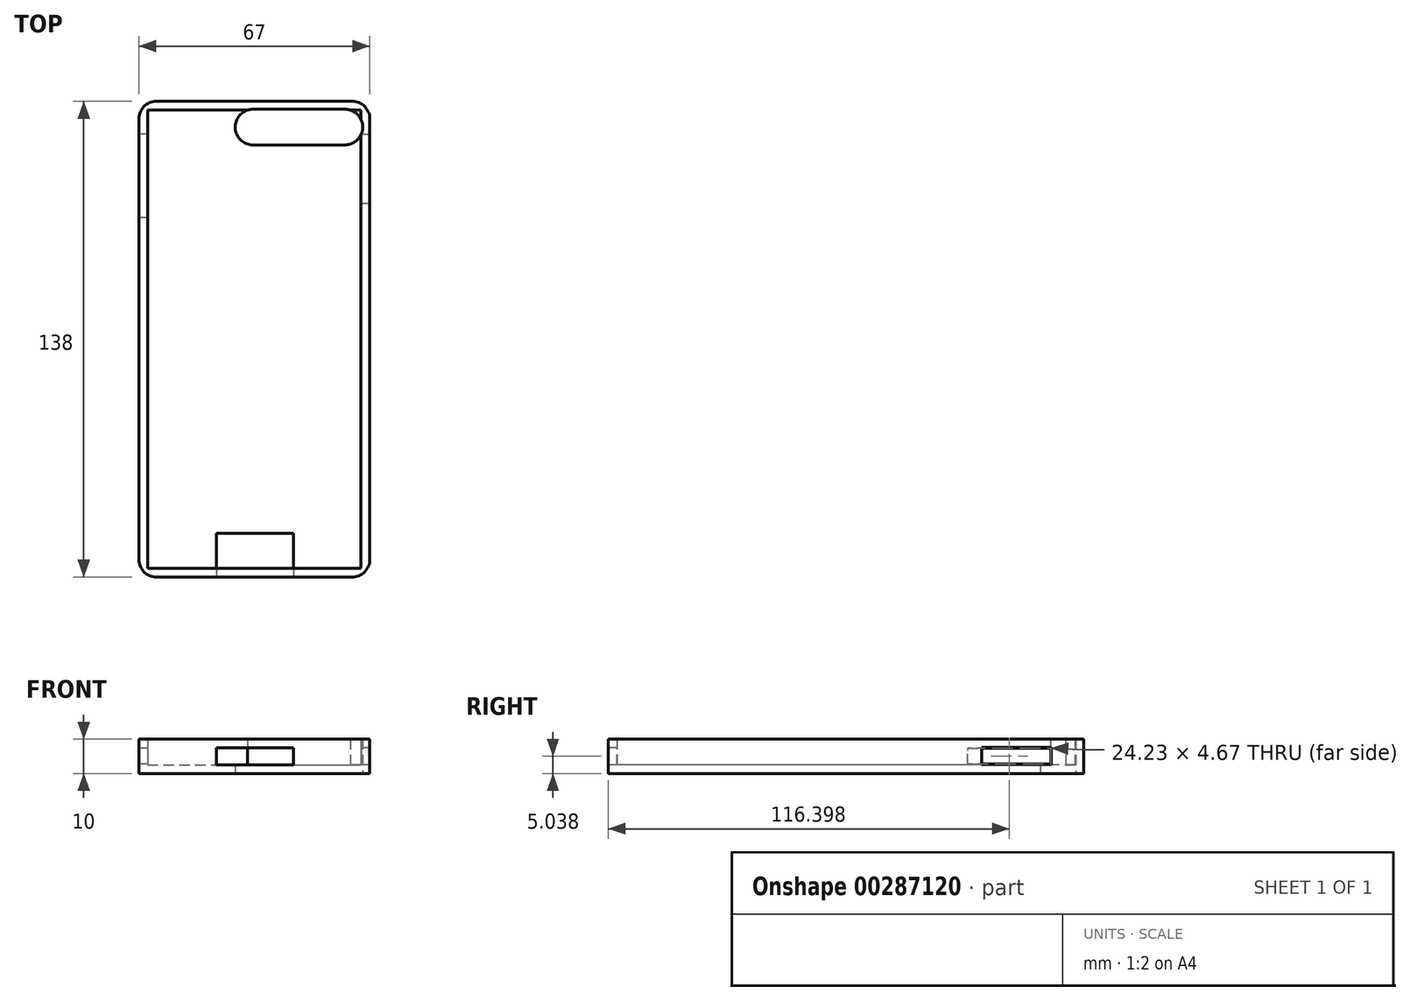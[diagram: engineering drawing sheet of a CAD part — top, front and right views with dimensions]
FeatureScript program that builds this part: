
annotation { "Feature Type Name" : "Feature", "Feature Type Description" : "" }
export const myFeature = defineFeature(function(context is Context, id is Id, definition is map)
    precondition{}
    {
        {
            var Q0;
            Q0=qCreatedBy(makeId("Top.planeOp"),FACE);
            var sketch = newSketch(context, id + "F0", { "sketchPlane" : qUnion([Q0])});
            skLineSegment(sketch, "E0.bottom", {"start": v(-44.89, 63.82) * mm, "end": v(22.11, 63.82) * mm});
            skLineSegment(sketch, "E0.top", {"start": v(-44.89, -74.18) * mm, "end": v(22.11, -74.18) * mm});
            skLineSegment(sketch, "E0.left", {"start": v(-44.89, 63.82) * mm, "end": v(-44.89, -74.18) * mm});
            skLineSegment(sketch, "E0.right", {"start": v(22.11, 63.82) * mm, "end": v(22.11, -74.18) * mm});
            skSolve(sketch);
        }
        {
            var Q0;
            Q0=makeQuery(id+"F0.imprint","IMPRINT",FACE,{"disambiguationData":[TD([[makeQuery(id+"F0.imprint","IMPRINT",EDGE,{"derivedFrom":sQuery(id+"F0.wireOp",EDGE,"E0.bottom")}),-1.0]])]});
            extrude(context, id + "F1", {"entities" : qUnion([Q0]), "depth" : 10 * mm});
        }
        {
            var Q0;
            Q0=makeQuery(id+"F1.opExtrude","CAP_FACE",FACE,{"disambiguationData":[OSD([sQuery(id+"F0.wireOp",EDGE,"E0.bottom"),sQuery(id+"F0.wireOp",EDGE,"E0.top"),sQuery(id+"F0.wireOp",EDGE,"E0.left"),sQuery(id+"F0.wireOp",EDGE,"E0.right")])],"isStart":false});
            shell(context, id + "F2", {"entities" : qUnion([Q0]), "thickness" : 2.54 * mm});
        }
        {
            var Q0;
            Q0=makeQuery(id+"F1.opExtrude","SWEPT_EDGE",EDGE,{"disambiguationData":[OSD([sQuery(id+"F0.wireOp",EDGE,"E0.bottom"),sQuery(id+"F0.wireOp",EDGE,"E0.left")])]});
            fillet(context, id + "F3", {"entities" : qUnion([Q0]), "radius" : 5.08 * mm, "tangentPropagation" : true, "allowEdgeOverflow" : false});
        }
        {
            var Q0;
            Q0=makeQuery(id+"F1.opExtrude","SWEPT_EDGE",EDGE,{"disambiguationData":[OSD([sQuery(id+"F0.wireOp",EDGE,"E0.bottom"),sQuery(id+"F0.wireOp",EDGE,"E0.right")])]});
            fillet(context, id + "F4", {"entities" : qUnion([Q0]), "radius" : 5.08 * mm, "tangentPropagation" : true, "allowEdgeOverflow" : false});
        }
        {
            var Q0;
            Q0=makeQuery(id+"F1.opExtrude","SWEPT_EDGE",EDGE,{"disambiguationData":[OSD([sQuery(id+"F0.wireOp",EDGE,"E0.top"),sQuery(id+"F0.wireOp",EDGE,"E0.right")])]});
            fillet(context, id + "F5", {"entities" : qUnion([Q0]), "radius" : 5.08 * mm, "tangentPropagation" : true, "allowEdgeOverflow" : false});
        }
        {
            var Q0;
            Q0=makeQuery(id+"F1.opExtrude","SWEPT_EDGE",EDGE,{"disambiguationData":[OSD([sQuery(id+"F0.wireOp",EDGE,"E0.top"),sQuery(id+"F0.wireOp",EDGE,"E0.left")])]});
            fillet(context, id + "F6", {"entities" : qUnion([Q0]), "radius" : 5.08 * mm, "tangentPropagation" : true, "allowEdgeOverflow" : false});
        }
        {
            var Q0;
            Q0=makeQuery(id+"F1.opExtrude","CAP_FACE",FACE,{"disambiguationData":[OSD([sQuery(id+"F0.wireOp",EDGE,"E0.bottom"),sQuery(id+"F0.wireOp",EDGE,"E0.top"),sQuery(id+"F0.wireOp",EDGE,"E0.left"),sQuery(id+"F0.wireOp",EDGE,"E0.right")])],"isStart":true});
            var sketch = newSketch(context, id + "F7", { "sketchPlane" : qUnion([Q0])});
            skLineSegment(sketch, "E1.bottom", {"start": v(14.88, -61.52) * mm, "end": v(-11.74, -61.52) * mm});
            skLineSegment(sketch, "E1.top", {"start": v(14.88, -51.16) * mm, "end": v(-11.74, -51.16) * mm});
            skLineSegment(sketch, "E1.left", {"start": v(14.88, -61.52) * mm, "end": v(14.88, -51.16) * mm});
            skLineSegment(sketch, "E1.right", {"start": v(-11.74, -61.52) * mm, "end": v(-11.74, -51.16) * mm});
            skArc(sketch, "E2", {"start": v(14.88, -61.52) * mm, "mid": v(20.06, -56.34) * mm, "end": v(14.88, -51.16) * mm});
            skArc(sketch, "E3", {"start": v(-11.74, -51.16) * mm, "mid": v(-16.92, -56.34) * mm, "end": v(-11.74, -61.52) * mm});
            skSolve(sketch);
        }
        {
            var Q0;
            Q0=makeQuery(id+"F7.imprint","IMPRINT",FACE,{"disambiguationData":[TD([[makeQuery(id+"F7.imprint","IMPRINT",EDGE,{"derivedFrom":sQuery(id+"F7.wireOp",EDGE,"E1.bottom")}),-1.0]])]});
            var Q1;
            Q1=makeQuery(id+"F7.imprint","IMPRINT",FACE,{"disambiguationData":[TD([[makeQuery(id+"F7.imprint","IMPRINT",EDGE,{"derivedFrom":sQuery(id+"F7.wireOp",EDGE,"E1.left")}),-1.0]])]});
            var Q2;
            Q2=makeQuery(id+"F7.imprint","IMPRINT",FACE,{"disambiguationData":[TD([[makeQuery(id+"F7.imprint","IMPRINT",EDGE,{"derivedFrom":sQuery(id+"F7.wireOp",EDGE,"E1.right")}),1.0]])]});
            extrude(context, id + "F8", {"entities" : qUnion([Q0, Q1, Q2]), "operationType" : NewBodyOperationType.REMOVE, "oppositeDirection" : true, "depth" : 25.4 * mm});
        }
        {
            var Q0;
            Q0=makeQuery(id+"F1.opExtrude","SWEPT_FACE",FACE,{"disambiguationData":[OSD([sQuery(id+"F0.wireOp",EDGE,"E0.top")])]});
            var sketch = newSketch(context, id + "F9", { "sketchPlane" : qUnion([Q0])});
            skLineSegment(sketch, "E4.bottom", {"start": v(-22.44, 7.43) * mm, "end": v(0, 7.43) * mm});
            skLineSegment(sketch, "E4.top", {"start": v(-22.44, 2.48) * mm, "end": v(0, 2.48) * mm});
            skLineSegment(sketch, "E4.left", {"start": v(-22.44, 7.43) * mm, "end": v(-22.44, 2.48) * mm});
            skLineSegment(sketch, "E4.right", {"start": v(0, 7.43) * mm, "end": v(0, 2.48) * mm});
            skSolve(sketch);
        }
        {
            var Q0;
            Q0=makeQuery(id+"F9.imprint","IMPRINT",FACE,{"disambiguationData":[TD([[makeQuery(id+"F9.imprint","IMPRINT",EDGE,{"derivedFrom":sQuery(id+"F9.wireOp",EDGE,"E4.bottom")}),-1.0]])]});
            extrude(context, id + "F10", {"entities" : qUnion([Q0]), "operationType" : NewBodyOperationType.REMOVE, "endBound" : BoundingType.SYMMETRIC, "oppositeDirection" : true, "depth" : 25.4 * mm});
        }
        {
            var Q0;
            Q0=makeQuery(id+"F1.opExtrude","SWEPT_FACE",FACE,{"disambiguationData":[OSD([sQuery(id+"F0.wireOp",EDGE,"E0.left")])]});
            var sketch = newSketch(context, id + "F11", { "sketchPlane" : qUnion([Q0])});
            skLineSegment(sketch, "E5.bottom", {"start": v(-54.33, 2.7) * mm, "end": v(-30.1, 2.7) * mm});
            skLineSegment(sketch, "E5.top", {"start": v(-54.33, 7.37) * mm, "end": v(-30.1, 7.37) * mm});
            skLineSegment(sketch, "E5.left", {"start": v(-54.33, 2.7) * mm, "end": v(-54.33, 7.37) * mm});
            skLineSegment(sketch, "E5.right", {"start": v(-30.1, 2.7) * mm, "end": v(-30.1, 7.37) * mm});
            skSolve(sketch);
        }
        {
            var Q0;
            Q0=makeQuery(id+"F11.imprint","IMPRINT",FACE,{"disambiguationData":[TD([[makeQuery(id+"F11.imprint","IMPRINT",EDGE,{"derivedFrom":sQuery(id+"F11.wireOp",EDGE,"E5.bottom")}),1.0]])]});
            extrude(context, id + "F12", {"entities" : qUnion([Q0]), "operationType" : NewBodyOperationType.REMOVE, "oppositeDirection" : true, "depth" : 25.4 * mm});
        }
        {
            var Q0;
            Q0=makeQuery(id+"F1.opExtrude","SWEPT_FACE",FACE,{"disambiguationData":[OSD([sQuery(id+"F0.wireOp",EDGE,"E0.right")])]});
            var sketch = newSketch(context, id + "F13", { "sketchPlane" : qUnion([Q0])});
            skLineSegment(sketch, "E6.bottom", {"start": v(54.36, 7.58) * mm, "end": v(34.25, 7.58) * mm});
            skLineSegment(sketch, "E6.top", {"start": v(54.36, 2.62) * mm, "end": v(34.25, 2.62) * mm});
            skLineSegment(sketch, "E6.left", {"start": v(54.36, 7.58) * mm, "end": v(54.36, 2.62) * mm});
            skLineSegment(sketch, "E6.right", {"start": v(34.25, 7.58) * mm, "end": v(34.25, 2.62) * mm});
            skSolve(sketch);
        }
        {
            var Q0;
            Q0=makeQuery(id+"F13.imprint","IMPRINT",FACE,{"disambiguationData":[TD([[makeQuery(id+"F13.imprint","IMPRINT",EDGE,{"derivedFrom":sQuery(id+"F13.wireOp",EDGE,"E6.bottom")}),1.0]])]});
            extrude(context, id + "F14", {"entities" : qUnion([Q0]), "operationType" : NewBodyOperationType.REMOVE, "oppositeDirection" : true, "depth" : 25.4 * mm});
        }
    });
